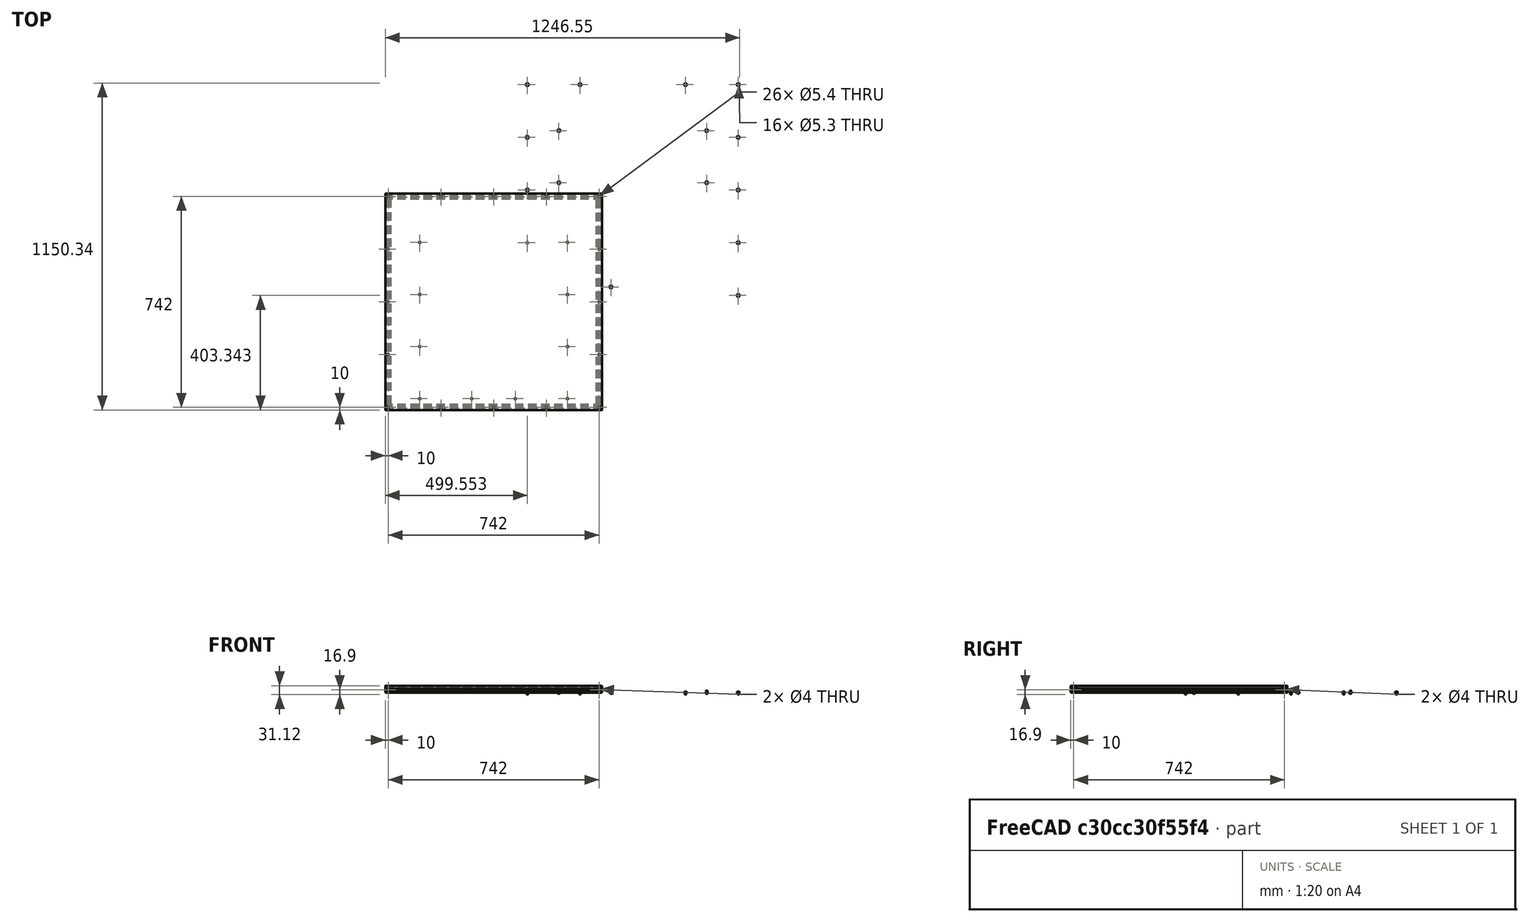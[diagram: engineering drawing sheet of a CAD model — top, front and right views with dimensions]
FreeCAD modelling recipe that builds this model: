
FCSTD DOCUMENT  (FreeCAD 0.17R8073 (Git))
Label: TAZ6_frame_full_assy
License: CreativeCommons Attribution-ShareAlike
LicenseURL: http://creativecommons.org/licenses/by-sa/4.0/
objects: Part::FeaturePython×39, App::FeaturePython×27, Drawing::FeatureViewPython×10, Drawing::FeatureViewPart×6, Drawing::FeaturePage×4
note: 39 computed .brp shape members not serialized (recipe doc carries the construction recipe); baked Part::Feature solids carry a one-line shape summary decoded from their .brp

FEATURE [Part::FeaturePython] _62mm_extrusion_01  # a2plus imported part (geometry in sourceFile) (typed FeaturePython)
  Placement = pos=(0,0,0) rot=(0.57735,0.57735,0.57735;2.0944rad)
  fixedPosition = true
  sourceFile = <userpath>/shared-j/devel/lulzbot/TAZ/Olive/production_parts/jigs/TAZ6_frame_assy_fixture/762mm_extrusion.fcstd
  timeLastImport = 1468502701
  updateColors = true
FEATURE [Part::FeaturePython] _62mm_extrusion_01001  # a2plus imported part (geometry in sourceFile) (typed FeaturePython)
  Placement = pos=(-1e-12,742,0) rot=(0.57735,0.57735,0.57735;2.0944rad)
  fixedPosition = false
  sourceFile = <userpath>/shared-j/devel/lulzbot/TAZ/Olive/production_parts/jigs/TAZ6_frame_assy_fixture/762mm_extrusion.fcstd
  timeLastImport = 1468502701
  updateColors = true
FEATURE [Part::FeaturePython] _22mm_extrusion_01  # a2plus imported part (geometry in sourceFile) (typed FeaturePython)
  Placement = pos=(-752,732,0) rot=(0,0.707107,0.707107;3.14159rad)
  fixedPosition = false
  sourceFile = <userpath>/shared-j/devel/lulzbot/TAZ/Olive/production_parts/jigs/TAZ6_frame_assy_fixture/722mm_extrusion.fcstd
  timeLastImport = 1468502835
  updateColors = true
FEATURE [Part::FeaturePython] _22mm_extrusion_01001  # a2plus imported part (geometry in sourceFile) (typed FeaturePython)
  Placement = pos=(-10,10,0) rot=(1,0,0;1.5708rad)
  fixedPosition = false
  sourceFile = <userpath>/shared-j/devel/lulzbot/TAZ/Olive/production_parts/jigs/TAZ6_frame_assy_fixture/722mm_extrusion.fcstd
  timeLastImport = 1468502835
  updateColors = true
FEATURE [App::FeaturePython] planeConstraint01_mirror  label="planeConstraint01_"  # a2plus constraint (typed FeaturePython)
  Object1 = _62mm_extrusion_01
  Object2 = Fillet
  SubElement1 = Face23
  SubElement2 = Face10
  Type = plane
  directionConstraint = 1
  offset = 0
FEATURE [App::FeaturePython] planeConstraint02_mirror  label="planeConstraint02_"  # a2plus constraint (typed FeaturePython)
  Object1 = _62mm_extrusion_01
  Object2 = Fillet
  SubElement1 = Face26
  SubElement2 = Face49
  Type = plane
  directionConstraint = 1
  offset = 0
FEATURE [App::FeaturePython] planeConstraint03_mirror  label="planeConstraint03_"  # a2plus constraint (typed FeaturePython)
  Object1 = _62mm_extrusion_01
  Object2 = Fillet
  SubElement1 = Face2
  SubElement2 = Face7
  Type = plane
  directionConstraint = 0
  offset = 0
FEATURE [App::FeaturePython] planeConstraint04_mirror  label="planeConstraint04_"  # a2plus constraint (typed FeaturePython)
  Object1 = Fillet
  Object2 = _62mm_extrusion_01001
  SubElement1 = Face10
  SubElement2 = Face1
  Type = plane
  directionConstraint = 1
  offset = 0
FEATURE [App::FeaturePython] planeConstraint05_mirror  label="planeConstraint05_"  # a2plus constraint (typed FeaturePython)
  Object1 = _62mm_extrusion_01001
  Object2 = Fillet
  SubElement1 = Face27
  SubElement2 = Face1
  Type = plane
  directionConstraint = 1
  offset = 0
FEATURE [App::FeaturePython] planeConstraint06_mirror  label="planeConstraint06_"  # a2plus constraint (typed FeaturePython)
  Object1 = _62mm_extrusion_01001
  Object2 = Fillet
  SubElement1 = Face5
  SubElement2 = Face13
  Type = plane
  directionConstraint = 0
  offset = 0
FEATURE [App::FeaturePython] planeConstraint07_mirror  label="planeConstraint07_"  # a2plus constraint (typed FeaturePython)
  Object1 = _22mm_extrusion_01
  Object2 = Fillet
  SubElement1 = Face1
  SubElement2 = Face10
  Type = plane
  directionConstraint = 1
  offset = 0
FEATURE [App::FeaturePython] planeConstraint08_mirror  label="planeConstraint08_"  # a2plus constraint (typed FeaturePython)
  Object1 = _22mm_extrusion_01
  Object2 = Fillet
  SubElement1 = Face27
  SubElement2 = Face13
  Type = plane
  directionConstraint = 1
  offset = 0
FEATURE [App::FeaturePython] planeConstraint09  # a2plus constraint (typed FeaturePython)
  Object1 = _62mm_extrusion_01001
  Object2 = _22mm_extrusion_01
  SubElement1 = Face6
  SubElement2 = Face2
  Type = plane
  directionConstraint = 0
  offset = 0
FEATURE [App::FeaturePython] planeConstraint09_mirror  label="planeConstraint09_"  # a2plus constraint (typed FeaturePython)
  Object1 = _62mm_extrusion_01001
  Object2 = _22mm_extrusion_01
  SubElement1 = Face6
  SubElement2 = Face2
  Type = plane
  directionConstraint = 0
  offset = 0
FEATURE [App::FeaturePython] planeConstraint10_mirror  label="planeConstraint10_"  # a2plus constraint (typed FeaturePython)
  Object1 = Fillet
  Object2 = _22mm_extrusion_01001
  SubElement1 = Face10
  SubElement2 = Face1
  Type = plane
  directionConstraint = 1
  offset = 0
FEATURE [App::FeaturePython] planeConstraint11_mirror  label="planeConstraint11_"  # a2plus constraint (typed FeaturePython)
  Object1 = _22mm_extrusion_01001
  Object2 = Fillet
  SubElement1 = Face27
  SubElement2 = Face7
  Type = plane
  directionConstraint = 1
  offset = 0
FEATURE [App::FeaturePython] planeConstraint12  # a2plus constraint (typed FeaturePython)
  Object1 = _22mm_extrusion_01001
  Object2 = _62mm_extrusion_01
  SubElement1 = Face2
  SubElement2 = Face47
  Type = plane
  directionConstraint = 0
  offset = 0
FEATURE [App::FeaturePython] planeConstraint12_mirror  label="planeConstraint12_"  # a2plus constraint (typed FeaturePython)
  Object1 = _22mm_extrusion_01001
  Object2 = _62mm_extrusion_01
  SubElement1 = Face2
  SubElement2 = Face47
  Type = plane
  directionConstraint = 0
  offset = 0
FEATURE [Part::FeaturePython] Washer  label="M5-Washer197"  # Fasteners workbench fastener (typed FeaturePython)
  Placement = pos=(-262.447,578.843,-10) rot=(0,0,1;0rad)
  diameter = 1
  invert = false
  matchOuter = false
  offset = 0
  type = 1
FEATURE [Part::FeaturePython] Washer001  label="M5-Washer"  # Fasteners workbench fastener (typed FeaturePython)
  Placement = pos=(368.553,973.343,-10) rot=(1,0,0;3.14159rad)
  diameter = 1
  invert = false
  matchOuter = false
  offset = 0
  type = 1
FEATURE [Part::FeaturePython] Washer002  label="M5-Washer196"  # Fasteners workbench fastener (typed FeaturePython)
  Placement = pos=(-151.447,973.343,-10) rot=(1,0,0;3.14159rad)
  diameter = 1
  invert = false
  matchOuter = false
  offset = 0
  type = 1
FEATURE [Part::FeaturePython] Washer003  label="M5-Washer198"  # Fasteners workbench fastener (typed FeaturePython)
  Placement = pos=(368.553,790.01,-10) rot=(1,0,0;3.14159rad)
  diameter = 1
  invert = false
  matchOuter = false
  offset = 0
  type = 1
FEATURE [Part::FeaturePython] Washer004  label="M5-Washer210"  # Fasteners workbench fastener (typed FeaturePython)
  Placement = pos=(294.053,1135.34,-10) rot=(0,0,1;0rad)
  diameter = 1
  invert = false
  matchOuter = false
  offset = 0
  type = 1
FEATURE [Part::FeaturePython] Washer005  label="M5-Washer209"  # Fasteners workbench fastener (typed FeaturePython)
  Placement = pos=(-262.447,1135.34,-10) rot=(0,0,1;0rad)
  diameter = 1
  invert = false
  matchOuter = false
  offset = 0
  type = 1
FEATURE [Part::FeaturePython] Washer006  label="M5-Washer208"  # Fasteners workbench fastener (typed FeaturePython)
  Placement = pos=(-151.447,790.01,-10) rot=(1,0,0;3.14159rad)
  diameter = 1
  invert = false
  matchOuter = false
  offset = 0
  type = 1
FEATURE [Part::FeaturePython] Washer007  label="M5-Washer207"  # Fasteners workbench fastener (typed FeaturePython)
  Placement = pos=(-76.9471,1135.34,-10) rot=(0,0,1;0rad)
  diameter = 1
  invert = false
  matchOuter = false
  offset = 0
  type = 1
FEATURE [Part::FeaturePython] Washer008  label="M5-Washer206"  # Fasteners workbench fastener (typed FeaturePython)
  Placement = pos=(-262.447,949.843,-10) rot=(0,0,1;0rad)
  diameter = 1
  invert = false
  matchOuter = false
  offset = 0
  type = 1
FEATURE [Part::FeaturePython] Washer009  label="M5-Washer205"  # Fasteners workbench fastener (typed FeaturePython)
  Placement = pos=(479.553,764.343,-10) rot=(0,0,1;0rad)
  diameter = 1
  invert = false
  matchOuter = false
  offset = 0
  type = 1
FEATURE [Part::FeaturePython] Washer010  label="M5-Washer204"  # Fasteners workbench fastener (typed FeaturePython)
  Placement = pos=(479.553,578.843,-10) rot=(0,0,1;0rad)
  diameter = 1
  invert = false
  matchOuter = false
  offset = 0
  type = 1
FEATURE [Part::FeaturePython] Washer011  label="M5-Washer203"  # Fasteners workbench fastener (typed FeaturePython)
  Placement = pos=(479.553,1135.34,-10) rot=(0,0,1;0rad)
  diameter = 1
  invert = false
  matchOuter = false
  offset = 0
  type = 1
FEATURE [Part::FeaturePython] Washer012  label="M5-Washer202"  # Fasteners workbench fastener (typed FeaturePython)
  Placement = pos=(479.553,949.843,-10) rot=(0,0,1;0rad)
  diameter = 1
  invert = false
  matchOuter = false
  offset = 0
  type = 1
FEATURE [Part::FeaturePython] Washer013  label="M5-Washer201"  # Fasteners workbench fastener (typed FeaturePython)
  Placement = pos=(479.553,393.343,-10) rot=(0,0,1;0rad)
  diameter = 1
  invert = false
  matchOuter = false
  offset = 0
  type = 1
FEATURE [Part::FeaturePython] Washer014  label="M5-Washer200"  # Fasteners workbench fastener (typed FeaturePython)
  Placement = pos=(31.8863,423.343,-10) rot=(1,0,0;3.14159rad)
  diameter = 1
  invert = false
  matchOuter = false
  offset = 0
  type = 1
FEATURE [Part::FeaturePython] Washer015  label="M5-Washer199"  # Fasteners workbench fastener (typed FeaturePython)
  Placement = pos=(-262.447,764.343,-10) rot=(0,0,1;0rad)
  diameter = 1
  invert = false
  matchOuter = false
  offset = 0
  type = 1
FEATURE [Part::FeaturePython] Screw  label="M5x8-Screw"  # Fasteners workbench fastener (typed FeaturePython)
  Placement = pos=(368.553,973.343,-11.1) rot=(1,0,0;3.14159rad)
  baseObject = -> Washer001 [Edge1]
  diameter = 3
  invert = false
  length = 0
  matchOuter = false
  offset = 0
  thread = false
  type = 20
FEATURE [Part::FeaturePython] Screw001  label="M5x8-Screw205"  # Fasteners workbench fastener (typed FeaturePython)
  Placement = pos=(-151.447,973.343,-11.1) rot=(1,0,0;3.14159rad)
  baseObject = -> Washer002 [Edge1]
  diameter = 3
  invert = false
  length = 0
  matchOuter = false
  offset = 0
  thread = false
  type = 20
FEATURE [Part::FeaturePython] Screw003  label="M5x8-Screw206"  # Fasteners workbench fastener (typed FeaturePython)
  Placement = pos=(-262.447,578.843,-8.9) rot=(0,0,1;0rad)
  baseObject = -> Washer [Edge1]
  diameter = 3
  invert = false
  length = 0
  matchOuter = false
  offset = 0
  thread = false
  type = 20
FEATURE [Part::FeaturePython] Screw006  label="M5x8-Screw207"  # Fasteners workbench fastener (typed FeaturePython)
  Placement = pos=(368.553,790.01,-11.1) rot=(1,0,0;3.14159rad)
  baseObject = -> Washer003 [Edge1]
  diameter = 3
  invert = false
  length = 0
  matchOuter = false
  offset = 0
  thread = false
  type = 20
FEATURE [Part::FeaturePython] Screw008  label="M5x8-Screw208"  # Fasteners workbench fastener (typed FeaturePython)
  Placement = pos=(-262.447,764.343,-8.9) rot=(0,0,1;0rad)
  baseObject = -> Washer015 [Edge1]
  diameter = 3
  invert = false
  length = 0
  matchOuter = false
  offset = 0
  thread = false
  type = 20
FEATURE [Part::FeaturePython] Screw009  label="M5x8-Screw209"  # Fasteners workbench fastener (typed FeaturePython)
  Placement = pos=(31.8863,423.343,-11.1) rot=(1,0,0;3.14159rad)
  baseObject = -> Washer014 [Edge1]
  diameter = 3
  invert = false
  length = 0
  matchOuter = false
  offset = 0
  thread = false
  type = 20
FEATURE [Part::FeaturePython] Screw011  label="M5x8-Screw210"  # Fasteners workbench fastener (typed FeaturePython)
  Placement = pos=(479.553,393.343,-8.9) rot=(0,0,1;0rad)
  baseObject = -> Washer013 [Edge1]
  diameter = 3
  invert = false
  length = 0
  matchOuter = false
  offset = 0
  thread = false
  type = 20
FEATURE [Part::FeaturePython] Screw012  label="M5x8-Screw211"  # Fasteners workbench fastener (typed FeaturePython)
  Placement = pos=(479.553,949.843,-8.9) rot=(0,0,1;0rad)
  baseObject = -> Washer012 [Edge1]
  diameter = 3
  invert = false
  length = 0
  matchOuter = false
  offset = 0
  thread = false
  type = 20
FEATURE [Part::FeaturePython] Screw013  label="M5x8-Screw212"  # Fasteners workbench fastener (typed FeaturePython)
  Placement = pos=(479.553,1135.34,-8.9) rot=(0,0,1;0rad)
  baseObject = -> Washer011 [Edge1]
  diameter = 3
  invert = false
  length = 0
  matchOuter = false
  offset = 0
  thread = false
  type = 20
FEATURE [Part::FeaturePython] Screw014  label="M5x8-Screw213"  # Fasteners workbench fastener (typed FeaturePython)
  Placement = pos=(479.553,578.843,-8.9) rot=(0,0,1;0rad)
  baseObject = -> Washer010 [Edge1]
  diameter = 3
  invert = false
  length = 0
  matchOuter = false
  offset = 0
  thread = false
  type = 20
FEATURE [Part::FeaturePython] Screw015  label="M5x8-Screw214"  # Fasteners workbench fastener (typed FeaturePython)
  Placement = pos=(479.553,764.343,-8.9) rot=(0,0,1;0rad)
  baseObject = -> Washer009 [Edge1]
  diameter = 3
  invert = false
  length = 0
  matchOuter = false
  offset = 0
  thread = false
  type = 20
FEATURE [Part::FeaturePython] Screw017  label="M5x8-Screw215"  # Fasteners workbench fastener (typed FeaturePython)
  Placement = pos=(-262.447,949.843,-8.9) rot=(0,0,1;0rad)
  baseObject = -> Washer008 [Edge1]
  diameter = 3
  invert = false
  length = 0
  matchOuter = false
  offset = 0
  thread = false
  type = 20
FEATURE [Part::FeaturePython] Screw019  label="M5x8-Screw216"  # Fasteners workbench fastener (typed FeaturePython)
  Placement = pos=(-76.9471,1135.34,-8.9) rot=(0,0,1;0rad)
  baseObject = -> Washer007 [Edge1]
  diameter = 3
  invert = false
  length = 0
  matchOuter = false
  offset = 0
  thread = false
  type = 20
FEATURE [Part::FeaturePython] Screw021  label="M5x8-Screw217"  # Fasteners workbench fastener (typed FeaturePython)
  Placement = pos=(-151.447,790.01,-11.1) rot=(1,0,0;3.14159rad)
  baseObject = -> Washer006 [Edge1]
  diameter = 3
  invert = false
  length = 0
  matchOuter = false
  offset = 0
  thread = false
  type = 20
FEATURE [Part::FeaturePython] Screw023  label="M5x8-Screw218"  # Fasteners workbench fastener (typed FeaturePython)
  Placement = pos=(-262.447,1135.34,-8.9) rot=(0,0,1;0rad)
  baseObject = -> Washer005 [Edge1]
  diameter = 3
  invert = false
  length = 0
  matchOuter = false
  offset = 0
  thread = false
  type = 20
FEATURE [Part::FeaturePython] Screw024  label="M5x8-Screw219"  # Fasteners workbench fastener (typed FeaturePython)
  Placement = pos=(294.053,1135.34,-8.9) rot=(0,0,1;0rad)
  baseObject = -> Washer004 [Edge1]
  diameter = 3
  invert = false
  length = 0
  matchOuter = false
  offset = 0
  thread = false
  type = 20
FEATURE [App::FeaturePython] planeConstraint13_mirror  label="planeConstraint13_"  # a2plus constraint (typed FeaturePython)
  Object1 = TAZ6_frame_assy_fixture_base_plate_01
  Object2 = muxedAssembly
  SubElement1 = Face10
  SubElement2 = Face103
  Type = plane
  directionConstraint = 1
  offset = 0
FEATURE [App::FeaturePython] planeConstraint14_mirror  label="planeConstraint14_"  # a2plus constraint (typed FeaturePython)
  Object1 = TAZ6_frame_assy_fixture_base_plate_01
  Object2 = muxedAssembly
  SubElement1 = Face49
  SubElement2 = Face6
  Type = plane
  directionConstraint = 1
  offset = 0
FEATURE [App::FeaturePython] planeConstraint15_mirror  label="planeConstraint15_"  # a2plus constraint (typed FeaturePython)
  Object1 = TAZ6_frame_assy_fixture_base_plate_01
  Object2 = muxedAssembly
  SubElement1 = Face7
  SubElement2 = Face180
  Type = plane
  directionConstraint = 1
  offset = 0
FEATURE [Part::FeaturePython] TAZ6_frame_assy_fixture_01  # a2plus imported part (geometry in sourceFile) (typed FeaturePython)
  Placement = pos=(-148,-8,24.2225) rot=(0,0,1;0rad)
  fixedPosition = false
  sourceFile = <userpath>/shared-j/devel/lulzbot/TAZ/Olive/production_parts/jigs/TAZ6_frame_assy_fixture/TAZ6_frame_assy_fixture.fcstd
  timeLastImport = 1465248702
  updateColors = true
FEATURE [App::FeaturePython] planeConstraint13_mirror001  label="planeConstraint13_001"  # a2plus constraint (typed FeaturePython)
  Object1 = Fillet
  Object2 = _22mm_extrusion_01001
  SubElement1 = Face10
  SubElement2 = Face1
  Type = plane
  directionConstraint = 0
  offset = 0
FEATURE [Part::FeaturePython] muxedAssembly  # WARN: FeaturePython — macro-defined, semantics opaque (R4)
  type = muxedAssembly
FEATURE [App::FeaturePython] planeConstraint15_mirror001  label="planeConstraint15_001"  # a2plus constraint (typed FeaturePython)
  Object1 = TAZ6_frame_assy_fixture_base_plate_01
  Object2 = muxedAssembly
  SubElement1 = Face12
  SubElement2 = Face560
  Type = plane
  directionConstraint = 0
  offset = 0
FEATURE [App::FeaturePython] planeConstraint16_mirror  label="planeConstraint16_"  # a2plus constraint (typed FeaturePython)
  Object1 = TAZ6_frame_assy_fixture_base_plate_01
  Object2 = muxedAssembly
  SubElement1 = Face49
  SubElement2 = Face6
  Type = plane
  directionConstraint = 1
  offset = 0
FEATURE [App::FeaturePython] planeConstraint17_mirror  label="planeConstraint17_"  # a2plus constraint (typed FeaturePython)
  Object1 = TAZ6_frame_assy_fixture_base_plate_01
  Object2 = muxedAssembly
  SubElement1 = Face7
  SubElement2 = Face180
  Type = plane
  directionConstraint = 1
  offset = 0
FEATURE [Part::FeaturePython] TAZ6_frame_assy_fixture_base_plate_01  # a2plus imported part (geometry in sourceFile) (typed FeaturePython)
  Placement = pos=(-489.553,-393.343,24.2225) rot=(0,0,1;0rad)
  fixedPosition = false
  sourceFile = <userpath>/shared-j/devel/lulzbot/TAZ/Olive/production_parts/jigs/TAZ6_frame_assy_fixture/TAZ6_frame_assy_fixture_base_plate.fcstd
  timeLastImport = 1468601354
  updateColors = true
FEATURE [App::FeaturePython] planeConstraint15  # a2plus constraint (typed FeaturePython)
  Object1 = TAZ6_frame_assy_fixture_base_plate_01
  Object2 = muxedAssembly
  SubElement1 = Face12
  SubElement2 = Face458
  Type = plane
  directionConstraint = 0
  offset = 0
FEATURE [App::FeaturePython] planeConstraint15_mirror002  label="planeConstraint15_002"  # a2plus constraint (typed FeaturePython)
  Object1 = TAZ6_frame_assy_fixture_base_plate_01
  Object2 = muxedAssembly
  SubElement1 = Face12
  SubElement2 = Face458
  Type = plane
  directionConstraint = 0
  offset = 0
FEATURE [App::FeaturePython] planeConstraint01  # a2plus constraint (typed FeaturePython)
  Object1 = TAZ6_frame_assy_fixture_base_plate_01
  Object2 = muxedAssembly
  SubElement1 = Face13
  SubElement2 = Face129
  Type = plane
  directionConstraint = 1
  offset = 0
FEATURE [App::FeaturePython] planeConstraint01_mirror001  label="planeConstraint01_001"  # a2plus constraint (typed FeaturePython)
  Object1 = TAZ6_frame_assy_fixture_base_plate_01
  Object2 = muxedAssembly
  SubElement1 = Face13
  SubElement2 = Face129
  Type = plane
  directionConstraint = 1
  offset = 0
FEATURE [App::FeaturePython] planeConstraint02  # a2plus constraint (typed FeaturePython)
  Object1 = TAZ6_frame_assy_fixture_base_plate_01
  Object2 = muxedAssembly
  SubElement1 = Face49
  SubElement2 = Face6
  Type = plane
  directionConstraint = 1
  offset = 0
FEATURE [App::FeaturePython] planeConstraint02_mirror001  label="planeConstraint02_001"  # a2plus constraint (typed FeaturePython)
  Object1 = TAZ6_frame_assy_fixture_base_plate_01
  Object2 = muxedAssembly
  SubElement1 = Face49
  SubElement2 = Face6
  Type = plane
  directionConstraint = 1
  offset = 0
FEATURE [Drawing::FeatureViewPython] dimPartsList01  # drawing view (typed FeaturePython)
  Rotation = 0
  ViewResult = <blob: 2555 chars omitted>
  Visible = true
  X = 135
  Y = 5
FEATURE [Drawing::FeatureViewPart] Ortho001  label="Ortho_1_1"
  Direction = (0.57735,0.57735,0.57735)
  HiddenWidth = 0.15
  LineWidth = 0.35
  Rotation = 120
  Scale = 0.175
  ShowHiddenLines = false
  ShowSmoothLines = false
  Source = -> muxedAssembly
  Tolerance = 0.05
  ViewResult = <blob: 65407 chars omitted>
  Visible = true
  X = 33.3511
  Y = 109.071
FEATURE [Drawing::FeaturePage] Page001
  EditableTexts = Turbo | 07/15/2016 | N/A | TAZ frame fixture | IR | Drawing number | 1 of 4
  Group = -> [dimPartsList01,Ortho001]
  Template = <path>
FEATURE [Drawing::FeatureViewPart] Ortho002  label="Ortho_0_1"
  Direction = (0,0,1)
  HiddenWidth = 0.15
  LineWidth = 0.35
  Rotation = 90
  Scale = 0.125
  ShowHiddenLines = false
  ShowSmoothLines = false
  Source = -> TAZ6_frame_assy_fixture_base_plate_01
  Tolerance = 0.05
  ViewResult = <g id="Ortho_0_1"\n   transform="rotate(90,93.325,155.575) translate(93.325,155.575) scale(0.125,0.125)"\n  >\n<g   stroke="rgb(0, 0, 0)"\n   stroke-width="2.8"\n   stroke-linecap="butt"\n   stroke-linejoin="miter"\n   fill="none"\n   transform="scale(1,-1)"\n  >\n<path id= "1" d=" M -761 752 L -1 752 " />\n<path id= "2" d=" M -9.09495e-13 751 L -9.09495e-13 -9 " />\n<path d="M-1 752 A1 1 0 0 0 -9.09495e-13 751" /><path d="M-761 752 A1 1 0 0 1 -762 751" /><circle cx ="-641" cy ="30" r ="2.7" /><circle cx ="-641" cy ="213.333" r ="2.7" /><circle cx ="-752" cy ="371" r ="2.7" /><circle cx ="-752" cy ="185.5" r ="2.7" /><circle cx ="-381" cy ="0" r ="2.7" /><circle cx ="-566.5" cy ="0" r ="2.7" /><circle cx ="-457.667" cy ="30" r ="2.7" /><circle cx ="-752" cy ="0" r ="2.7" /><circle cx ="-121" cy ="213.333" r ="2.7" /><circle cx ="-195.5" cy ="0" r ="2.7" /><circle cx ="-121" cy ="30" r ="2.7" /><circle cx ="-304.333" cy ="30" r ="2.7" /><circle cx ="-381" cy ="742" r ="2.7" /><circle cx ="-195.5" cy ="742" r ="2.7" /><circle cx ="-121" cy ="396.667" r ="2.7" /><circle cx ="-121" cy ="580" r ="2.7" /><circle cx ="-641" cy ="580" r ="2.7" /><circle cx ="-641" cy ="396.667" r ="2.7" /><circle cx ="-566.5" cy ="742" r ="2.7" /><circle cx ="-752" cy ="742" r ="2.7" /><circle cx ="-752" cy ="556.5" r ="2.7" /><circle cx ="-10" cy ="371" r ="2.7" /><circle cx ="-10" cy ="185.5" r ="2.7" /><circle cx ="-10" cy ="556.5" r ="2.7" /><circle cx ="-10" cy ="742" r ="2.7" /><circle cx ="-10" cy ="0" r ="2.7" /><path id= "31" d=" M -762 -9 L -762 751 " />\n<path id= "32" d=" M -1 -10 L -761 -10 " />\n<path d="M-9.09495e-13 -9 A1 1 0 0 0 -1 -10" /><path d="M-762 -9 A1 1 0 0 1 -761 -10" /><path d="M-762 -9 A1 1 0 0 1 -761 -10" /></g>\n</g>
  Visible = true
  X = 93.325
  Y = 155.575
FEATURE [Drawing::FeatureViewPart] Ortho  label="Ortho_0_0"
  Direction = (1,0,0)
  HiddenWidth = 0.15
  LineWidth = 0.35
  Rotation = -90
  Scale = 0.25
  ShowHiddenLines = false
  ShowSmoothLines = false
  Source = -> _62mm_extrusion_01
  Tolerance = 0.05
  ViewResult = <blob: 2445 chars omitted>
  Visible = true
  X = 39.6667
  Y = 81.5
FEATURE [Drawing::FeatureViewPart] Ortho003  label="Ortho_1_0"
  Direction = (0,1,0)
  HiddenWidth = 0.15
  LineWidth = 0.35
  Rotation = -90
  Scale = 0.25
  ShowHiddenLines = false
  ShowSmoothLines = false
  Source = -> _62mm_extrusion_01
  Tolerance = 0.05
  ViewResult = <blob: 3977 chars omitted>
  Visible = true
  X = 69.3333
  Y = 81.5
FEATURE [Drawing::FeatureViewPython] dim001  # drawing view (typed FeaturePython)
  Rotation = 0
  ViewResult = <g> \n  <line x1="37.166700" y1="77.750000" x2="37.166700" y2="69.000000" style="stroke:rgb(0,0,255);stroke-width:0.20" />\n<line x1="42.166700" y1="77.750000" x2="42.166700" y2="69.000000" style="stroke:rgb(0,0,255);stroke-width:0.20" />\n<line x1="37.166700" y1="70.000000" x2="42.166700" y2="70.000000" style="stroke:rgb(0,0,255);stroke-width:0.20" /> \n  <polygon points="42.166700,70.000000 45.166700,70.750000 45.166700,70.000000 45.166700,69.250000" style="fill:rgb(0,0,255);stroke:rgb(0,0,255);stroke-width:0" /><polygon points="37.166700,70.000000 34.166700,69.250000 34.166700,70.000000 34.166700,70.750000" style="fill:rgb(0,0,255);stroke:rgb(0,0,255);stroke-width:0" /> \n  <text x="39.666700" y="70.000000" font-family="Verdana" font-size="3.6" fill="rgb(0,0,255)" text-anchor="middle" transform="rotate(0.000000 39.666700,70.000000)" >20</text> </g>
  Visible = true
  X = 0
  Y = 0
  arrowL1 = 3
  arrowL2 = 0
  arrowW = 1.5
  arrow_scheme = 0
  autoPlaceOffset = 0
  autoPlaceText = true
  click1_x = 40
  click1_y = 70
  click2_x = 40
  click2_y = 70
  comma_decimal_place = false
  dimension_line_overshoot = 1
  gap_datum_points = 1.5
  halfDimension_linear = false
  lineColor = rgb(0,0,255)
  strokeWidth = 0.2
  textFormat_linear = %(value)3.3f
  textRenderer_color = rgb(0,0,255)
  textRenderer_family = Verdana
  textRenderer_size = 3.6
  unit_custom_scale = 1
  unit_scheme = 0
FEATURE [Drawing::FeatureViewPython] dim002  # drawing view (typed FeaturePython)
  Rotation = 0
  ViewResult = <g> \n  <line x1="35.916700" y1="79.000000" x2="29.000000" y2="79.000000" style="stroke:rgb(0,0,255);stroke-width:0.20" />\n<line x1="35.916700" y1="84.000000" x2="29.000000" y2="84.000000" style="stroke:rgb(0,0,255);stroke-width:0.20" />\n<line x1="30.000000" y1="79.000000" x2="30.000000" y2="84.000000" style="stroke:rgb(0,0,255);stroke-width:0.20" /> \n  <polygon points="30.000000,84.000000 29.250000,87.000000 30.000000,87.000000 30.750000,87.000000" style="fill:rgb(0,0,255);stroke:rgb(0,0,255);stroke-width:0" /><polygon points="30.000000,79.000000 30.750000,76.000000 30.000000,76.000000 29.250000,76.000000" style="fill:rgb(0,0,255);stroke:rgb(0,0,255);stroke-width:0" /> \n  <text x="30.000000" y="81.500000" font-family="Verdana" font-size="3.6" fill="rgb(0,0,255)" text-anchor="middle" transform="rotate(-90.000000 30.000000,81.500000)" >20</text> </g>
  Visible = true
  X = 0
  Y = 0
  arrowL1 = 3
  arrowL2 = 0
  arrowW = 1.5
  arrow_scheme = 0
  autoPlaceOffset = 0
  autoPlaceText = true
  click1_x = 30
  click1_y = 80
  click2_x = 30
  click2_y = 80
  comma_decimal_place = false
  dimension_line_overshoot = 1
  gap_datum_points = 1.5
  halfDimension_linear = false
  lineColor = rgb(0,0,255)
  strokeWidth = 0.2
  textFormat_linear = %(value)3.3f
  textRenderer_color = rgb(0,0,255)
  textRenderer_family = Verdana
  textRenderer_size = 3.6
  unit_custom_scale = 1
  unit_scheme = 0
FEATURE [Drawing::FeatureViewPython] dim003  # drawing view (typed FeaturePython)
  Rotation = 0
  ViewResult = <g> \n  <line x1="69.333300" y1="80.781250" x2="69.333300" y2="69.000000" style="stroke:rgb(0,0,255);stroke-width:0.20" />\n<line x1="259.833300" y1="80.781250" x2="259.833300" y2="69.000000" style="stroke:rgb(0,0,255);stroke-width:0.20" />\n<line x1="69.333300" y1="70.000000" x2="259.833300" y2="70.000000" style="stroke:rgb(0,0,255);stroke-width:0.20" /> \n  <polygon points="259.833300,70.000000 256.833300,69.250000 256.833300,70.000000 256.833300,70.750000" style="fill:rgb(0,0,255);stroke:rgb(0,0,255);stroke-width:0" /><polygon points="69.333300,70.000000 72.333300,70.750000 72.333300,70.000000 72.333300,69.250000" style="fill:rgb(0,0,255);stroke:rgb(0,0,255);stroke-width:0" /> \n  <text x="164.583300" y="70.000000" font-family="Verdana" font-size="3.6" fill="rgb(0,0,255)" text-anchor="middle" transform="rotate(0.000000 164.583300,70.000000)" >762</text> </g>
  Visible = true
  X = 0
  Y = 0
  arrowL1 = 3
  arrowL2 = 0
  arrowW = 1.5
  arrow_scheme = 0
  autoPlaceOffset = 0
  autoPlaceText = true
  click1_x = 100
  click1_y = 70
  click2_x = 100
  click2_y = 70
  comma_decimal_place = false
  dimension_line_overshoot = 1
  gap_datum_points = 1.5
  halfDimension_linear = false
  lineColor = rgb(0,0,255)
  strokeWidth = 0.2
  textFormat_linear = %(value)3.3f
  textRenderer_color = rgb(0,0,255)
  textRenderer_family = Verdana
  textRenderer_size = 3.6
  unit_custom_scale = 1
  unit_scheme = 0
FEATURE [Drawing::FeaturePage] Page002
  EditableTexts = Designed by Name | Date | Scale | 762mm etrusion | IR | Drawing number | 3 of 4
  Group = -> [Ortho,Ortho003,dim001,dim002,dim003]
  Template = <path>
FEATURE [Drawing::FeatureViewPart] Ortho004  label="Ortho_0_002"
  Direction = (1,0,0)
  HiddenWidth = 0.15
  LineWidth = 0.35
  Rotation = -90
  Scale = 0.25
  ShowHiddenLines = false
  ShowSmoothLines = false
  Source = -> _22mm_extrusion_01001
  Tolerance = 0.05
  ViewResult = <blob: 2756 chars omitted>
  Visible = true
  X = 38
  Y = 81.5
FEATURE [Drawing::FeatureViewPart] Ortho005  label="Ortho_1_002"
  Direction = (0,1,0)
  HiddenWidth = 0.15
  LineWidth = 0.35
  Rotation = -90
  Scale = 0.25
  ShowHiddenLines = false
  ShowSmoothLines = false
  Source = -> _22mm_extrusion_01001
  Tolerance = 0.05
  ViewResult = <blob: 2615 chars omitted>
  Visible = true
  X = 251.5
  Y = 81.5
FEATURE [Drawing::FeatureViewPython] dim004  # drawing view (typed FeaturePython)
  Rotation = 0
  ViewResult = <g> \n  <line x1="40.500000" y1="79.250000" x2="40.500000" y2="54.000000" style="stroke:rgb(0,0,255);stroke-width:0.20" />\n<line x1="221.000000" y1="80.055982" x2="221.000000" y2="54.000000" style="stroke:rgb(0,0,255);stroke-width:0.20" />\n<line x1="40.500000" y1="55.000000" x2="221.000000" y2="55.000000" style="stroke:rgb(0,0,255);stroke-width:0.20" /> \n  <polygon points="221.000000,55.000000 218.000000,54.250000 218.000000,55.000000 218.000000,55.750000" style="fill:rgb(0,0,255);stroke:rgb(0,0,255);stroke-width:0" /><polygon points="40.500000,55.000000 43.500000,55.750000 43.500000,55.000000 43.500000,54.250000" style="fill:rgb(0,0,255);stroke:rgb(0,0,255);stroke-width:0" /> \n  <text x="130.750000" y="55.000000" font-family="Verdana" font-size="3.6" fill="rgb(0,0,255)" text-anchor="middle" transform="rotate(0.000000 130.750000,55.000000)" >722</text> </g>
  Visible = true
  X = 0
  Y = 0
  arrowL1 = 3
  arrowL2 = 0
  arrowW = 1.5
  arrow_scheme = 0
  autoPlaceOffset = 0
  autoPlaceText = true
  click1_x = 205
  click1_y = 55
  click2_x = 205
  click2_y = 55
  comma_decimal_place = false
  dimension_line_overshoot = 1
  gap_datum_points = 1.5
  halfDimension_linear = false
  lineColor = rgb(0,0,255)
  strokeWidth = 0.2
  textFormat_linear = %(value)3.3f
  textRenderer_color = rgb(0,0,255)
  textRenderer_family = Verdana
  textRenderer_size = 3.6
  unit_custom_scale = 1
  unit_scheme = 0
FEATURE [Drawing::FeatureViewPython] dim005  # drawing view (typed FeaturePython)
  Rotation = 0
  ViewResult = <g> \n  <line x1="256.500000" y1="77.750000" x2="256.500000" y2="54.000000" style="stroke:rgb(0,0,255);stroke-width:0.20" />\n<line x1="251.500000" y1="77.750000" x2="251.500000" y2="54.000000" style="stroke:rgb(0,0,255);stroke-width:0.20" />\n<line x1="256.500000" y1="55.000000" x2="251.500000" y2="55.000000" style="stroke:rgb(0,0,255);stroke-width:0.20" /> \n  <polygon points="251.500000,55.000000 248.500000,54.250000 248.500000,55.000000 248.500000,55.750000" style="fill:rgb(0,0,255);stroke:rgb(0,0,255);stroke-width:0" /><polygon points="256.500000,55.000000 259.500000,55.750000 259.500000,55.000000 259.500000,54.250000" style="fill:rgb(0,0,255);stroke:rgb(0,0,255);stroke-width:0" /> \n  <text x="254.000000" y="55.000000" font-family="Verdana" font-size="3.6" fill="rgb(0,0,255)" text-anchor="middle" transform="rotate(-0.000000 254.000000,55.000000)" >20</text> </g>
  Visible = true
  X = 0
  Y = 0
  arrowL1 = 3
  arrowL2 = 0
  arrowW = 1.5
  arrow_scheme = 0
  autoPlaceOffset = 0
  autoPlaceText = true
  click1_x = 250
  click1_y = 55
  click2_x = 250
  click2_y = 55
  comma_decimal_place = false
  dimension_line_overshoot = 1
  gap_datum_points = 1.5
  halfDimension_linear = false
  lineColor = rgb(0,0,255)
  strokeWidth = 0.2
  textFormat_linear = %(value)3.3f
  textRenderer_color = rgb(0,0,255)
  textRenderer_family = Verdana
  textRenderer_size = 3.6
  unit_custom_scale = 1
  unit_scheme = 0
FEATURE [Drawing::FeatureViewPython] dim006  # drawing view (typed FeaturePython)
  Rotation = 0
  ViewResult = <g> \n  <line x1="257.750000" y1="79.000000" x2="271.000000" y2="79.000000" style="stroke:rgb(0,0,255);stroke-width:0.20" />\n<line x1="257.750000" y1="84.000000" x2="271.000000" y2="84.000000" style="stroke:rgb(0,0,255);stroke-width:0.20" />\n<line x1="270.000000" y1="79.000000" x2="270.000000" y2="84.000000" style="stroke:rgb(0,0,255);stroke-width:0.20" /> \n  <polygon points="270.000000,84.000000 269.250000,87.000000 270.000000,87.000000 270.750000,87.000000" style="fill:rgb(0,0,255);stroke:rgb(0,0,255);stroke-width:0" /><polygon points="270.000000,79.000000 270.750000,76.000000 270.000000,76.000000 269.250000,76.000000" style="fill:rgb(0,0,255);stroke:rgb(0,0,255);stroke-width:0" /> \n  <text x="270.000000" y="81.500000" font-family="Verdana" font-size="3.6" fill="rgb(0,0,255)" text-anchor="middle" transform="rotate(-90.000000 270.000000,81.500000)" >20</text> </g>
  Visible = true
  X = 0
  Y = 0
  arrowL1 = 3
  arrowL2 = 0
  arrowW = 1.5
  arrow_scheme = 0
  autoPlaceOffset = 0
  autoPlaceText = true
  click1_x = 270
  click1_y = 80
  click2_x = 270
  click2_y = 80
  comma_decimal_place = false
  dimension_line_overshoot = 1
  gap_datum_points = 1.5
  halfDimension_linear = false
  lineColor = rgb(0,0,255)
  strokeWidth = 0.2
  textFormat_linear = %(value)3.3f
  textRenderer_color = rgb(0,0,255)
  textRenderer_family = Verdana
  textRenderer_size = 3.6
  unit_custom_scale = 1
  unit_scheme = 0
FEATURE [Drawing::FeaturePage] Page003
  EditableTexts = Designed by Name | Date | Scale | 722mm extrusion | IR | Drawing number | 4 of 4
  Group = -> [Ortho004,Ortho005,dim004,dim005,dim006]
  Template = <path>
FEATURE [Drawing::FeatureViewPython] dimStack001  # drawing view (typed FeaturePython)
  Rotation = 0
  ViewResult = <blob: 5339 chars omitted>
  Visible = true
  X = 0
  Y = 0
  arrowL1 = 3
  arrowL2 = 0
  arrowW = 1.5
  arrow_scheme = 3
  autoPlaceOffset = 1
  click1_x = 102
  click1_y = 49
  comma_decimal_place = false
  dimension_line_overshoot = 1
  gap_datum_points = 1
  lineColor = rgb(0,0,255)
  stack_offset = 4
  stack_offset0 = 0
  strokeWidth = 0.2
  textFormat_linear = %(value)3.3f
  textRenderer_color = rgb(0,0,255)
  textRenderer_family = Verdana
  textRenderer_size = 3.6
  unit_custom_scale = 1
  unit_scheme = 0
FEATURE [Drawing::FeatureViewPython] dimStack002  # drawing view (typed FeaturePython)
  Rotation = 0
  ViewResult = <blob: 5344 chars omitted>
  Visible = true
  X = 0
  Y = 0
  arrowL1 = 3
  arrowL2 = 0
  arrowW = 1.5
  arrow_scheme = 3
  autoPlaceOffset = 1
  click1_x = 57
  click1_y = 94
  comma_decimal_place = false
  dimension_line_overshoot = 1
  gap_datum_points = 1
  lineColor = rgb(0,0,255)
  stack_offset = 4
  stack_offset0 = 0
  strokeWidth = 0.2
  textFormat_linear = %(value)3.3f
  textRenderer_color = rgb(0,0,255)
  textRenderer_family = Verdana
  textRenderer_size = 3.6
  unit_custom_scale = 1
  unit_scheme = 0
FEATURE [Drawing::FeatureViewPython] text002  # drawing view (typed FeaturePython)
  Rotation = 0
  ViewResult = <g> <text x="208.000000" y="16.000000" font-family="inherit" font-size="3.6" fill="rgb(0,0,0)" text-anchor="inherit" transform="rotate(0.000000 208.000000,16.000000)" >Note: Break all edges and corners</text> </g>
  Visible = true
  X = 0
  Y = 0
  click1_x = 208
  click1_y = 16
  rotation = 0
  text = Note: Break all edges and corners
  textRenderer_addText_color = rgb(0,0,0)
  textRenderer_addText_family = inherit
  textRenderer_addText_size = 3.6
FEATURE [Drawing::FeaturePage] Page
  EditableTexts = Turbo | .190" 6061 t6 | N/A | Base Plate | IR | Drawing number | 2 of 4
  Group = -> [Ortho002,dimStack001,dimStack002,text002]
  Template = <path>
note: 4 file-system paths scrubbed to <path> (originals preserved in the JSON sidecar)
